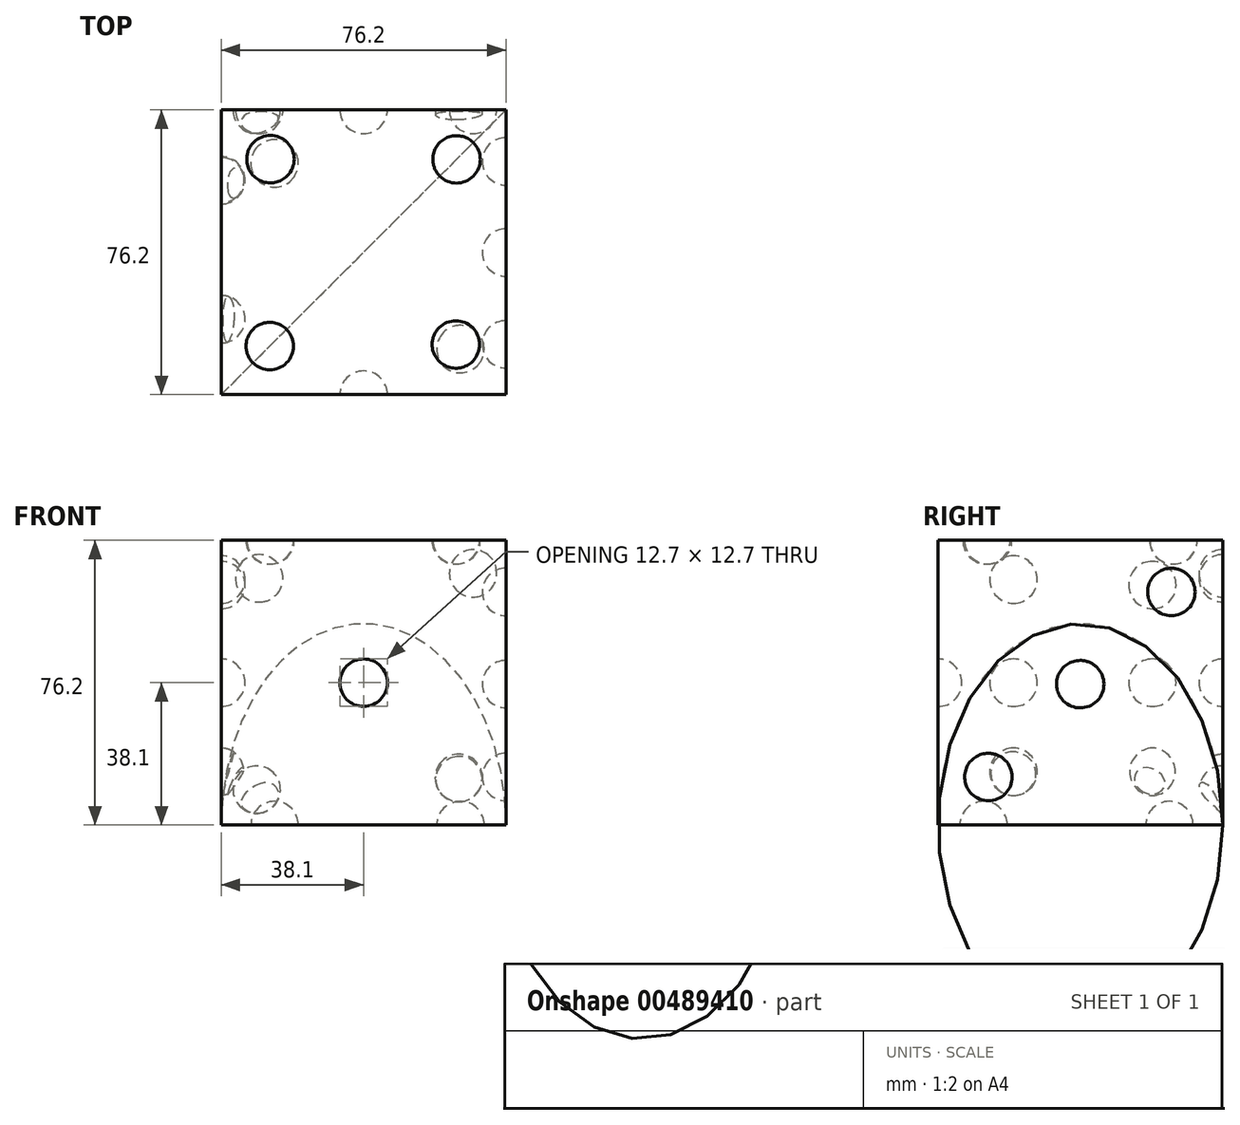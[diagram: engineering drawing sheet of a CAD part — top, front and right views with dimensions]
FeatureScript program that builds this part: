
annotation { "Feature Type Name" : "Feature", "Feature Type Description" : "" }
export const myFeature = defineFeature(function(context is Context, id is Id, definition is map)
    precondition{}
    {
        {
            var Q0;
            Q0=qCreatedBy(makeId("Front.planeOp"),FACE);
            var sketch = newSketch(context, id + "F0", { "sketchPlane" : qUnion([Q0])});
            skLineSegment(sketch, "E0", {"start": v(-76.2, 0) * mm, "end": v(0, 0) * mm});
            skLineSegment(sketch, "E1", {"start": v(0, 0) * mm, "end": v(0, 76.2) * mm});
            skLineSegment(sketch, "E2", {"start": v(0, 76.2) * mm, "end": v(-76.2, 76.2) * mm});
            skLineSegment(sketch, "E3", {"start": v(-76.2, 76.2) * mm, "end": v(-76.2, 0) * mm});
            skSolve(sketch);
        }
        {
            var Q0;
            Q0 = qSketchRegion(id + "F0", true);
            extrude(context, id + "F1", {"entities" : qUnion([Q0]), "depth" : 76.2 * mm});
        }
        {
            var Q0;
            Q0=makeQuery(id+"F1.opExtrude","CAP_FACE",FACE,{"disambiguationData":[OSD([sQuery(id+"F0.wireOp",EDGE,"E0"),sQuery(id+"F0.wireOp",EDGE,"E1"),sQuery(id+"F0.wireOp",EDGE,"E2"),sQuery(id+"F0.wireOp",EDGE,"E3")])],"isStart":false});
            var sketch = newSketch(context, id + "F2", { "sketchPlane" : qUnion([Q0])});
            skArc(sketch, "E4", {"start": v(-38.1, 31.75) * mm, "mid": v(-31.75, 38.1) * mm, "end": v(-38.1, 44.45) * mm});
            skPoint(sketch, "E5.orphan", {"position": v(-76.2, 76.2) * mm});
            skPoint(sketch, "E6.orphan", {"position": v(0, 0) * mm});
            skLineSegment(sketch, "E7", {"start": v(-38.1, 76.2) * mm, "end": v(-38.1, 0) * mm});
            skSolve(sketch);
        }
        {
            var Q0;
            Q0 = qSketchRegion(id + "F2", true);
            var Q1;
            Q1=sQuery(id+"F2.wireOp",EDGE,"E7");
            revolve(context, id + "F3", {"operationType" : NewBodyOperationType.REMOVE, "entities" : qUnion([Q0]), "axis" : qUnion([Q1]), "revolveType" : RevolveType.FULL, "oppositeDirection" : true});
        }
        {
            var Q0;
            Q0=qCreatedBy(makeId("Right.planeOp"),FACE);
            var sketch = newSketch(context, id + "F4", { "sketchPlane" : qUnion([Q0])});
            skLineSegment(sketch, "E8", {"start": v(0, 76.32) * mm, "end": v(-75.46, 0) * mm});
            skArc(sketch, "E9", {"start": v(-42.62, 33.21) * mm, "mid": v(-33.64, 33.26) * mm, "end": v(-33.7, 42.24) * mm});
            skArc(sketch, "E10", {"start": v(-18.23, 57.88) * mm, "mid": v(-9.25, 57.93) * mm, "end": v(-9.3, 66.9) * mm});
            skArc(sketch, "E11", {"start": v(-67.2, 8.36) * mm, "mid": v(-58.21, 8.4) * mm, "end": v(-58.26, 17.39) * mm});
            skPoint(sketch, "E12.orphan", {"position": v(0, 0) * mm});
            skSolve(sketch);
        }
        {
            var Q0;
            Q0=makeQuery(id+"F1.opExtrude","CAP_FACE",FACE,{"disambiguationData":[OSD([sQuery(id+"F0.wireOp",EDGE,"E0"),sQuery(id+"F0.wireOp",EDGE,"E1"),sQuery(id+"F0.wireOp",EDGE,"E2"),sQuery(id+"F0.wireOp",EDGE,"E3")])],"isStart":true});
            var sketch = newSketch(context, id + "F5", { "sketchPlane" : qUnion([Q0])});
            skLineSegment(sketch, "E13", {"start": v(0, 76.2) * mm, "end": v(76.2, 0) * mm});
            skArc(sketch, "E14", {"start": v(13.3, 62.9) * mm, "mid": v(13.3, 71.88) * mm, "end": v(4.32, 71.88) * mm});
            skArc(sketch, "E15", {"start": v(42.6, 33.6) * mm, "mid": v(42.6, 42.6) * mm, "end": v(33.6, 42.6) * mm});
            skArc(sketch, "E16", {"start": v(71.2, 5) * mm, "mid": v(71.2, 13.98) * mm, "end": v(62.22, 13.98) * mm});
            skPoint(sketch, "E17.orphan", {"position": v(76.2, 76.2) * mm});
            skPoint(sketch, "E18.start.orphan", {"position": v(0, 0) * mm});
            skSolve(sketch);
        }
        {
            var Q0;
            {var subQ0=sQuery(id+"F4.wireOp",EDGE,"E9");Q0=makeQuery(id+"F4.imprint","IMPRINT",FACE,{"disambiguationData":[TD([[makeQuery(id+"F4.imprint","IMPRINT",EDGE,{"derivedFrom":subQ0}),1.0]])]});}
            var Q1;
            {var subQ0=sQuery(id+"F4.wireOp",EDGE,"E10");Q1=makeQuery(id+"F4.imprint","IMPRINT",FACE,{"disambiguationData":[TD([[makeQuery(id+"F4.imprint","IMPRINT",EDGE,{"derivedFrom":subQ0}),1.0]])]});}
            var Q2;
            {var subQ0=sQuery(id+"F4.wireOp",EDGE,"E11");Q2=makeQuery(id+"F4.imprint","IMPRINT",FACE,{"disambiguationData":[TD([[makeQuery(id+"F4.imprint","IMPRINT",EDGE,{"derivedFrom":subQ0}),1.0]])]});}
            var Q3;
            Q3=sQuery(id+"F4.wireOp",EDGE,"E8");
            revolve(context, id + "F6", {"operationType" : NewBodyOperationType.REMOVE, "entities" : qUnion([Q0, Q1, Q2]), "axis" : qUnion([Q3]), "revolveType" : RevolveType.FULL, "oppositeDirection" : true});
        }
        {
            var Q0;
            {var subQ0=sQuery(id+"F5.wireOp",EDGE,"E14");Q0=makeQuery(id+"F5.imprint","IMPRINT",FACE,{"disambiguationData":[TD([[makeQuery(id+"F5.imprint","IMPRINT",EDGE,{"derivedFrom":subQ0}),1.0]])]});}
            var Q1;
            {var subQ0=sQuery(id+"F5.wireOp",EDGE,"E13");var subQ1=sQuery(id+"F5.wireOp",EDGE,"E18");var subQ2=makeQuery(id+"F5.imprint","INTERSECT",VERTEX,{"derivedFrom":[subQ1,subQ0]});Q1=makeQuery(id+"F5.imprint","IMPRINT",FACE,{"disambiguationData":[TD([[makeQuery(id+"F5.imprint","IMPRINT",EDGE,{"disambiguationData":[TD([[subQ2,-1.0]])],"derivedFrom":subQ1}),-1.0]])]});}
            var Q2;
            {var subQ0=sQuery(id+"F5.wireOp",EDGE,"E13");var subQ1=sQuery(id+"F5.wireOp",EDGE,"E18");var subQ2=makeQuery(id+"F5.imprint","INTERSECT",VERTEX,{"derivedFrom":[subQ1,subQ0]});Q2=makeQuery(id+"F5.imprint","IMPRINT",FACE,{"disambiguationData":[TD([[makeQuery(id+"F5.imprint","IMPRINT",EDGE,{"disambiguationData":[TD([[subQ2,-1.0]])],"derivedFrom":subQ1}),1.0]])]});}
            var Q3;
            {var subQ0=sQuery(id+"F5.wireOp",EDGE,"6EG49tWH-M61K-Isf9-N37i-THXrLgnY3K5K");Q3=makeQuery(id+"F5.imprint","IMPRINT",FACE,{"disambiguationData":[TD([[makeQuery(id+"F5.imprint","IMPRINT",EDGE,{"derivedFrom":subQ0}),1.0]])]});}
            var Q4;
            {var subQ0=sQuery(id+"F5.wireOp",EDGE,"E16");Q4=makeQuery(id+"F5.imprint","IMPRINT",FACE,{"disambiguationData":[TD([[makeQuery(id+"F5.imprint","IMPRINT",EDGE,{"derivedFrom":subQ0}),1.0]])]});}
            var Q5;
            {var subQ0=sQuery(id+"F5.wireOp",EDGE,"T0JHlIXA-7uEr-wneW-zrkr-TuRG13wyPwpN");Q5=makeQuery(id+"F5.imprint","IMPRINT",FACE,{"disambiguationData":[TD([[makeQuery(id+"F5.imprint","IMPRINT",EDGE,{"derivedFrom":subQ0}),1.0]])]});}
            var Q6;
            Q6=sQuery(id+"F5.wireOp",EDGE,"E13");
            revolve(context, id + "F7", {"operationType" : NewBodyOperationType.REMOVE, "entities" : qUnion([Q0, Q1, Q2, Q3, Q4, Q5]), "axis" : qUnion([Q6]), "revolveType" : RevolveType.FULL, "oppositeDirection" : true});
        }
        {
            var Q0;
            Q0=makeQuery(id+"F1.opExtrude","SWEPT_FACE",FACE,{"disambiguationData":[OSD([sQuery(id+"F0.wireOp",EDGE,"E0")])]});
            var sketch = newSketch(context, id + "F8", { "sketchPlane" : qUnion([Q0])});
            skLineSegment(sketch, "E19", {"start": v(-76.2, 76.2) * mm, "end": v(0, 0) * mm});
            skLineSegment(sketch, "E20", {"start": v(-76.2, 0) * mm, "end": v(0, 76.2) * mm});
            skCircle(sketch, "E21", {"center": v(-12.19, 64.01) * mm, "radius": 6.35 * mm});
            skCircle(sketch, "E22", {"center": v(-61.92, 14.28) * mm, "radius": 6.35 * mm});
            skSolve(sketch);
        }
        {
            var Q0;
            {var subQ0=sQuery(id+"F8.wireOp",EDGE,"E21");var subQ1=sQuery(id+"F8.wireOp",EDGE,"E20");var subQ2=makeQuery(id+"F8.imprint","INTERSECT",VERTEX,{"disambiguationData":[OD(0.0)],"derivedFrom":[subQ1,subQ0]});Q0=makeQuery(id+"F8.imprint","IMPRINT",FACE,{"disambiguationData":[TD([[makeQuery(id+"F8.imprint","IMPRINT",EDGE,{"disambiguationData":[TD([[subQ2,-1.0]])],"derivedFrom":subQ1}),-1.0]])]});}
            var Q1;
            {var subQ0=sQuery(id+"F8.wireOp",EDGE,"E22");var subQ1=sQuery(id+"F8.wireOp",EDGE,"E20");var subQ2=makeQuery(id+"F8.imprint","INTERSECT",VERTEX,{"disambiguationData":[OD(0.0)],"derivedFrom":[subQ1,subQ0]});Q1=makeQuery(id+"F8.imprint","IMPRINT",FACE,{"disambiguationData":[TD([[makeQuery(id+"F8.imprint","IMPRINT",EDGE,{"disambiguationData":[TD([[subQ2,-1.0]])],"derivedFrom":subQ1}),-1.0]])]});}
            var Q2;
            Q2=sQuery(id+"F8.wireOp",EDGE,"E20");
            revolve(context, id + "F9", {"operationType" : NewBodyOperationType.REMOVE, "entities" : qUnion([Q0, Q1]), "axis" : qUnion([Q2]), "revolveType" : RevolveType.FULL, "oppositeDirection" : true});
        }
        {
            var Q0;
            Q0=makeQuery(id+"F1.opExtrude","SWEPT_FACE",FACE,{"disambiguationData":[OSD([sQuery(id+"F0.wireOp",EDGE,"E2")])]});
            var sketch = newSketch(context, id + "F10", { "sketchPlane" : qUnion([Q0])});
            skLineSegment(sketch, "E23", {"start": v(0, -76.2) * mm, "end": v(-76.2, 0) * mm});
            skArc(sketch, "E24", {"start": v(-8.93, -67.27) * mm, "mid": v(-8.93, -58.29) * mm, "end": v(-17.91, -58.29) * mm});
            skArc(sketch, "E25", {"start": v(-58.54, -17.66) * mm, "mid": v(-58.54, -8.68) * mm, "end": v(-67.52, -8.68) * mm});
            skSolve(sketch);
        }
        {
            var Q0;
            Q0=makeQuery(id+"F1.opExtrude","CAP_FACE",FACE,{"disambiguationData":[OSD([sQuery(id+"F0.wireOp",EDGE,"E0"),sQuery(id+"F0.wireOp",EDGE,"E1"),sQuery(id+"F0.wireOp",EDGE,"E2"),sQuery(id+"F0.wireOp",EDGE,"E3")])],"isStart":true});
            var sketch = newSketch(context, id + "F11", { "sketchPlane" : qUnion([Q0])});
            skLineSegment(sketch, "E26", {"start": v(76.2, 76.2) * mm, "end": v(0, 0) * mm});
            skArc(sketch, "E27", {"start": v(61.55, 61.55) * mm, "mid": v(70.53, 61.55) * mm, "end": v(70.53, 70.53) * mm});
            skArc(sketch, "E28", {"start": v(33.6, 33.6) * mm, "mid": v(42.6, 33.6) * mm, "end": v(42.6, 42.6) * mm});
            skArc(sketch, "E29", {"start": v(8.13, 8.13) * mm, "mid": v(17.1, 8.13) * mm, "end": v(17.1, 17.1) * mm});
            skSolve(sketch);
        }
        {
            var Q0;
            {var subQ0=sQuery(id+"F11.wireOp",EDGE,"E28");Q0=makeQuery(id+"F11.imprint","IMPRINT",FACE,{"disambiguationData":[TD([[makeQuery(id+"F11.imprint","IMPRINT",EDGE,{"derivedFrom":subQ0}),1.0]])]});}
            var Q1;
            {var subQ0=sQuery(id+"F11.wireOp",EDGE,"E29");Q1=makeQuery(id+"F11.imprint","IMPRINT",FACE,{"disambiguationData":[TD([[makeQuery(id+"F11.imprint","IMPRINT",EDGE,{"derivedFrom":subQ0}),1.0]])]});}
            var Q2;
            {var subQ0=sQuery(id+"F11.wireOp",EDGE,"E27");Q2=makeQuery(id+"F11.imprint","IMPRINT",FACE,{"disambiguationData":[TD([[makeQuery(id+"F11.imprint","IMPRINT",EDGE,{"derivedFrom":subQ0}),1.0]])]});}
            var Q3;
            Q3=sQuery(id+"F11.wireOp",EDGE,"E26");
            revolve(context, id + "F12", {"operationType" : NewBodyOperationType.REMOVE, "entities" : qUnion([Q0, Q1, Q2]), "axis" : qUnion([Q3]), "revolveType" : RevolveType.FULL, "oppositeDirection" : true});
        }
        {
            var Q0;
            {var subQ0=sQuery(id+"F10.wireOp",EDGE,"E24");Q0=makeQuery(id+"F10.imprint","IMPRINT",FACE,{"disambiguationData":[TD([[makeQuery(id+"F10.imprint","IMPRINT",EDGE,{"derivedFrom":subQ0}),1.0]])]});}
            var Q1;
            {var subQ0=sQuery(id+"F10.wireOp",EDGE,"E25");Q1=makeQuery(id+"F10.imprint","IMPRINT",FACE,{"disambiguationData":[TD([[makeQuery(id+"F10.imprint","IMPRINT",EDGE,{"derivedFrom":subQ0}),1.0]])]});}
            var Q2;
            Q2=sQuery(id+"F10.wireOp",EDGE,"E23");
            revolve(context, id + "F13", {"operationType" : NewBodyOperationType.REMOVE, "entities" : qUnion([Q0, Q1]), "axis" : qUnion([Q2]), "revolveType" : RevolveType.FULL, "oppositeDirection" : true});
        }
        {
            var Q0;
            Q0=makeQuery(id+"F1.opExtrude","SWEPT_FACE",FACE,{"disambiguationData":[OSD([sQuery(id+"F0.wireOp",EDGE,"E2")])]});
            var sketch = newSketch(context, id + "F14", { "sketchPlane" : qUnion([Q0])});
            skLineSegment(sketch, "E30", {"start": v(0, 0) * mm, "end": v(-76.2, -76.2) * mm});
            skArc(sketch, "E31", {"start": v(-58.72, -58.72) * mm, "mid": v(-67.7, -58.72) * mm, "end": v(-67.7, -67.7) * mm});
            skArc(sketch, "E32", {"start": v(-8.74, -8.74) * mm, "mid": v(-17.72, -8.74) * mm, "end": v(-17.72, -17.72) * mm});
            skSolve(sketch);
        }
        {
            var Q0;
            {var subQ0=sQuery(id+"F14.wireOp",EDGE,"E31");Q0=makeQuery(id+"F14.imprint","IMPRINT",FACE,{"disambiguationData":[TD([[makeQuery(id+"F14.imprint","IMPRINT",EDGE,{"derivedFrom":subQ0}),1.0]])]});}
            var Q1;
            {var subQ0=sQuery(id+"F14.wireOp",EDGE,"E32");Q1=makeQuery(id+"F14.imprint","IMPRINT",FACE,{"disambiguationData":[TD([[makeQuery(id+"F14.imprint","IMPRINT",EDGE,{"derivedFrom":subQ0}),1.0]])]});}
            var Q2;
            Q2=sQuery(id+"F14.wireOp",EDGE,"E30");
            revolve(context, id + "F15", {"operationType" : NewBodyOperationType.REMOVE, "entities" : qUnion([Q0, Q1]), "axis" : qUnion([Q2]), "revolveType" : RevolveType.FULL, "oppositeDirection" : true});
        }
        {
            var Q0;
            Q0=makeQuery(id+"F1.opExtrude","SWEPT_FACE",FACE,{"disambiguationData":[OSD([sQuery(id+"F0.wireOp",EDGE,"E3")])]});
            var sketch = newSketch(context, id + "F16", { "sketchPlane" : qUnion([Q0])});
            skLineSegment(sketch, "E33", {"start": v(18.83, 76.2) * mm, "end": v(18.83, 0) * mm});
            skArc(sketch, "E34", {"start": v(18.83, 57.9) * mm, "mid": v(25.18, 64.25) * mm, "end": v(18.83, 70.6) * mm});
            skArc(sketch, "E35", {"start": v(18.83, 31.75) * mm, "mid": v(25.18, 38.1) * mm, "end": v(18.83, 44.45) * mm});
            skArc(sketch, "E36", {"start": v(18.83, 7.93) * mm, "mid": v(24.94, 14.28) * mm, "end": v(18.83, 20.62) * mm});
            skSolve(sketch);
        }
        {
            var Q0;
            {var subQ0=sQuery(id+"F16.wireOp",EDGE,"E34");Q0=makeQuery(id+"F16.imprint","IMPRINT",FACE,{"disambiguationData":[TD([[makeQuery(id+"F16.imprint","IMPRINT",EDGE,{"derivedFrom":subQ0}),1.0]])]});}
            var Q1;
            {var subQ0=sQuery(id+"F16.wireOp",EDGE,"E35");Q1=makeQuery(id+"F16.imprint","IMPRINT",FACE,{"disambiguationData":[TD([[makeQuery(id+"F16.imprint","IMPRINT",EDGE,{"derivedFrom":subQ0}),1.0]])]});}
            var Q2;
            {var subQ0=sQuery(id+"F16.wireOp",EDGE,"E36");Q2=makeQuery(id+"F16.imprint","IMPRINT",FACE,{"disambiguationData":[TD([[makeQuery(id+"F16.imprint","IMPRINT",EDGE,{"derivedFrom":subQ0}),1.0]])]});}
            var Q3;
            Q3=sQuery(id+"F16.wireOp",EDGE,"E33");
            revolve(context, id + "F17", {"operationType" : NewBodyOperationType.REMOVE, "entities" : qUnion([Q0, Q1, Q2]), "axis" : qUnion([Q3]), "revolveType" : RevolveType.FULL, "oppositeDirection" : true});
        }
        {
            var Q0;
            Q0=makeQuery(id+"F1.opExtrude","SWEPT_FACE",FACE,{"disambiguationData":[OSD([sQuery(id+"F0.wireOp",EDGE,"E3")])]});
            var sketch = newSketch(context, id + "F18", { "sketchPlane" : qUnion([Q0])});
            skLineSegment(sketch, "E37", {"start": v(56, 76.2) * mm, "end": v(56, 0) * mm});
            skArc(sketch, "E38", {"start": v(56, 59.38) * mm, "mid": v(62.36, 65.73) * mm, "end": v(56, 72.08) * mm});
            skArc(sketch, "E39", {"start": v(56, 31.75) * mm, "mid": v(62.36, 38.1) * mm, "end": v(56, 44.45) * mm});
            skArc(sketch, "E40", {"start": v(56, 7.93) * mm, "mid": v(62.36, 14.28) * mm, "end": v(56, 20.63) * mm});
            skSolve(sketch);
        }
        {
            var Q0;
            {var subQ0=sQuery(id+"F18.wireOp",EDGE,"E38");Q0=makeQuery(id+"F18.imprint","IMPRINT",FACE,{"disambiguationData":[TD([[makeQuery(id+"F18.imprint","IMPRINT",EDGE,{"derivedFrom":subQ0}),1.0]])]});}
            var Q1;
            {var subQ0=sQuery(id+"F18.wireOp",EDGE,"E39");Q1=makeQuery(id+"F18.imprint","IMPRINT",FACE,{"disambiguationData":[TD([[makeQuery(id+"F18.imprint","IMPRINT",EDGE,{"derivedFrom":subQ0}),1.0]])]});}
            var Q2;
            {var subQ0=sQuery(id+"F18.wireOp",EDGE,"E40");Q2=makeQuery(id+"F18.imprint","IMPRINT",FACE,{"disambiguationData":[TD([[makeQuery(id+"F18.imprint","IMPRINT",EDGE,{"derivedFrom":subQ0}),1.0]])]});}
            var Q3;
            Q3=sQuery(id+"F18.wireOp",EDGE,"E37");
            revolve(context, id + "F19", {"operationType" : NewBodyOperationType.REMOVE, "entities" : qUnion([Q0, Q1, Q2]), "axis" : qUnion([Q3]), "revolveType" : RevolveType.FULL, "oppositeDirection" : true});
        }
    });
